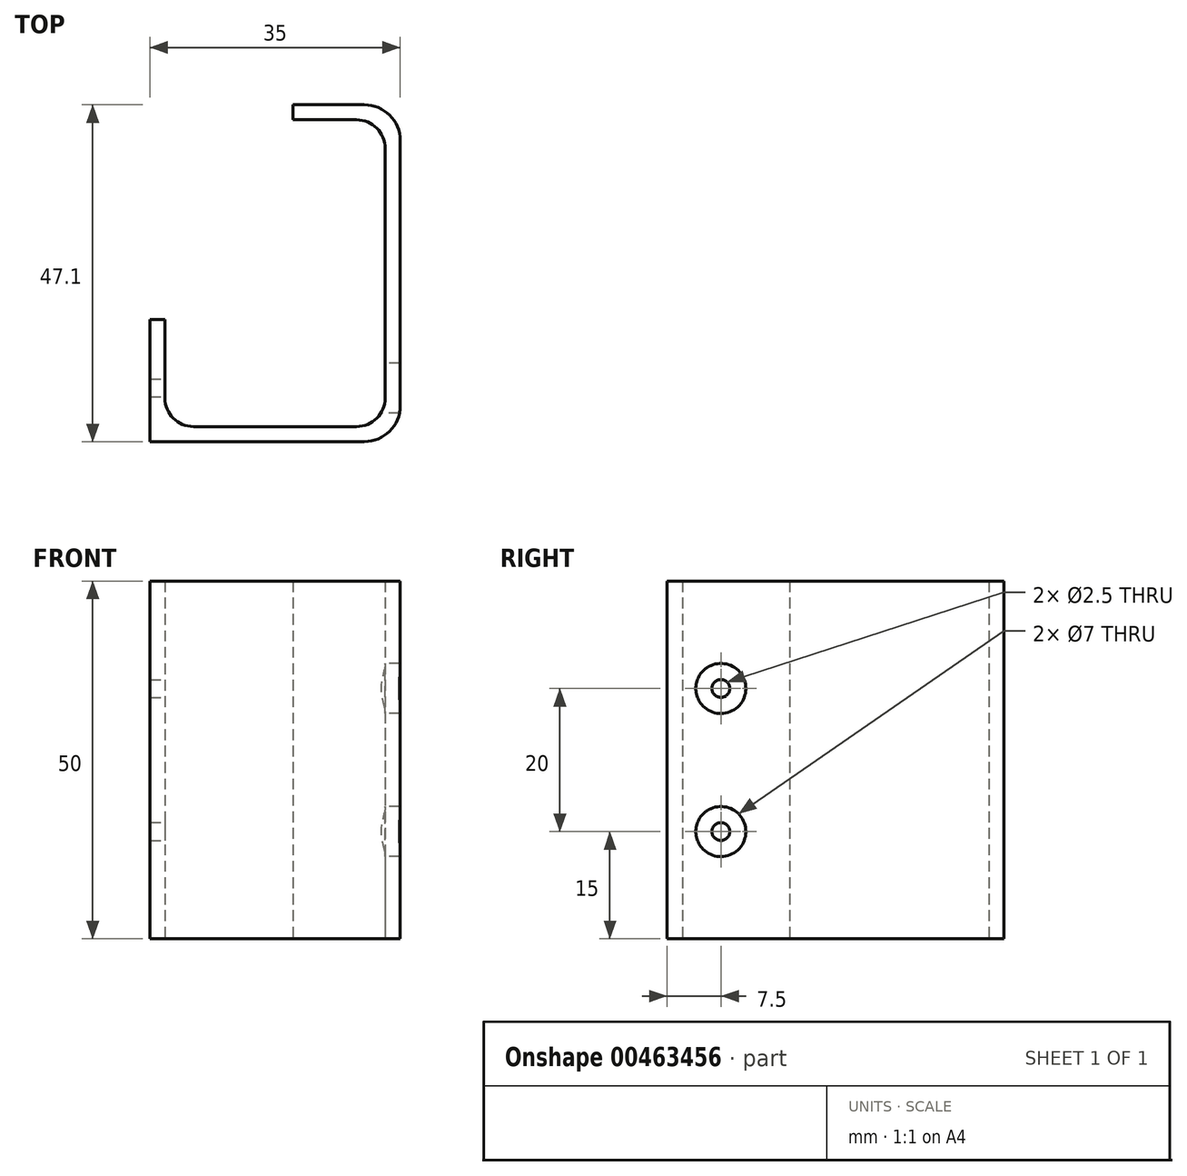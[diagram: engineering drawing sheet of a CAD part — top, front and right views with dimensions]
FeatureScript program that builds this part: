
annotation { "Feature Type Name" : "Feature", "Feature Type Description" : "" }
export const myFeature = defineFeature(function(context is Context, id is Id, definition is map)
    precondition{}
    {
        {
            var Q0;
            Q0=qCreatedBy(makeId("Top.planeOp"),FACE);
            var sketch = newSketch(context, id + "F0", { "sketchPlane" : qUnion([Q0])});
            skLineSegment(sketch, "E0", {"start": v(-4, 0) * mm, "end": v(-26.8, 0) * mm});
            skLineSegment(sketch, "E1", {"start": v(-30.8, 4) * mm, "end": v(-30.8, 45) * mm});
            skLineSegment(sketch, "E2", {"start": v(-30.8, 45) * mm, "end": v(-32.9, 45) * mm});
            skLineSegment(sketch, "E3", {"start": v(-32.9, 45) * mm, "end": v(-32.9, -2.1) * mm});
            skLineSegment(sketch, "E4", {"start": v(-32.9, -2.1) * mm, "end": v(2.1, -2.1) * mm});
            skLineSegment(sketch, "E5", {"start": v(2.1, -2.1) * mm, "end": v(2.1, 45) * mm});
            skPoint(sketch, "E6.end.orphan", {"position": v(14.76, 0) * mm});
            skLineSegment(sketch, "E7", {"start": v(2.1, 45) * mm, "end": v(-12.9, 45) * mm});
            skLineSegment(sketch, "E8", {"start": v(-12.9, 45) * mm, "end": v(-12.9, 42.9) * mm});
            skLineSegment(sketch, "E9", {"start": v(-12.9, 42.9) * mm, "end": v(-4, 42.9) * mm});
            skLineSegment(sketch, "E10", {"start": v(0, 38.9) * mm, "end": v(0, 4) * mm});
            skPoint(sketch, "E11.visualSharp", {"position": v(0, 42.9) * mm});
            skArc(sketch, "E11.filletArc", {"start": v(0, 38.9) * mm, "mid": v(-1.17, 41.73) * mm, "end": v(-4, 42.9) * mm});
            skPoint(sketch, "E12.visualSharp", {"position": v(-30.8, 0) * mm});
            skArc(sketch, "E12.filletArc", {"start": v(-30.8, 4) * mm, "mid": v(-29.63, 1.17) * mm, "end": v(-26.8, 0) * mm});
            skPoint(sketch, "E13.visualSharp", {"position": v(0, 0) * mm});
            skArc(sketch, "E13.filletArc", {"start": v(-4, 0) * mm, "mid": v(-1.17, 1.17) * mm, "end": v(0, 4) * mm});
            skLineSegment(sketch, "E14", {"start": v(-24.73, 0) * mm, "end": v(-24.73, 15) * mm, "construction": true});
            skLineSegment(sketch, "E15", {"start": v(-30.8, 15) * mm, "end": v(-32.9, 15) * mm});
            skSolve(sketch);
        }
        {
            var Q0;
            Q0=makeQuery(id+"F0.imprint","IMPRINT",FACE,{"disambiguationData":[TD([[makeQuery(id+"F0.imprint","IMPRINT",EDGE,{"derivedFrom":sQuery(id+"F0.wireOp",EDGE,"E0")}),1.0]])]});
            extrude(context, id + "F1", {"entities" : qUnion([Q0]), "depth" : 50 * mm});
        }
        {
            var Q0;
            Q0=qCreatedBy(makeId("Right.planeOp"),FACE);
            var sketch = newSketch(context, id + "F2", { "sketchPlane" : qUnion([Q0])});
            skLineSegment(sketch, "E16", {"start": v(0, 0) * mm, "end": v(5.4, 0) * mm, "construction": true});
            skLineSegment(sketch, "E17", {"start": v(5.4, 0) * mm, "end": v(5.4, 15) * mm, "construction": true});
            skLineSegment(sketch, "E18", {"start": v(5.4, 15) * mm, "end": v(5.4, 35) * mm, "construction": true});
            skLineSegment(sketch, "E19", {"start": v(5.4, 35) * mm, "end": v(5.4, 50) * mm, "construction": true});
            skCircle(sketch, "E20", {"center": v(5.4, 35) * mm, "radius": 1.25 * mm});
            skCircle(sketch, "E21", {"center": v(5.4, 15) * mm, "radius": 1.25 * mm});
            skCircle(sketch, "E22", {"center": v(5.4, 15) * mm, "radius": 3.5 * mm});
            skCircle(sketch, "E23", {"center": v(5.4, 35) * mm, "radius": 3.5 * mm});
            skSolve(sketch);
        }
        {
            var Q0;
            Q0=makeQuery(id+"F2.imprint","IMPRINT",FACE,{"disambiguationData":[TD([[makeQuery(id+"F2.imprint","IMPRINT",EDGE,{"derivedFrom":sQuery(id+"F2.wireOp",EDGE,"E20")}),1.0]])]});
            var Q1;
            Q1=makeQuery(id+"F2.imprint","IMPRINT",FACE,{"disambiguationData":[TD([[makeQuery(id+"F2.imprint","IMPRINT",EDGE,{"derivedFrom":sQuery(id+"F2.wireOp",EDGE,"E21")}),1.0]])]});
            extrude(context, id + "F3", {"entities" : qUnion([Q0, Q1]), "operationType" : NewBodyOperationType.REMOVE, "endBound" : BoundingType.THROUGH_ALL, "oppositeDirection" : true, "depth" : 25 * mm});
        }
        {
            var Q0;
            Q0=makeQuery(id+"F2.imprint","IMPRINT",FACE,{"disambiguationData":[TD([[makeQuery(id+"F2.imprint","IMPRINT",EDGE,{"derivedFrom":sQuery(id+"F2.wireOp",EDGE,"E20")}),-1.0]])]});
            var Q1;
            Q1=makeQuery(id+"F2.imprint","IMPRINT",FACE,{"disambiguationData":[TD([[makeQuery(id+"F2.imprint","IMPRINT",EDGE,{"derivedFrom":sQuery(id+"F2.wireOp",EDGE,"E21")}),-1.0]])]});
            var Q2;
            Q2=makeQuery(id+"F2.imprint","IMPRINT",FACE,{"disambiguationData":[TD([[makeQuery(id+"F2.imprint","IMPRINT",EDGE,{"derivedFrom":sQuery(id+"F2.wireOp",EDGE,"E21")}),1.0]])]});
            var Q3;
            Q3=makeQuery(id+"F2.imprint","IMPRINT",FACE,{"disambiguationData":[TD([[makeQuery(id+"F2.imprint","IMPRINT",EDGE,{"derivedFrom":sQuery(id+"F2.wireOp",EDGE,"E20")}),1.0]])]});
            extrude(context, id + "F4", {"entities" : qUnion([Q0, Q1, Q2, Q3]), "operationType" : NewBodyOperationType.REMOVE, "endBound" : BoundingType.UP_TO_NEXT, "depth" : 25 * mm, "hasSecondDirection" : true, "secondDirectionOppositeDirection" : true, "secondDirectionDepth" : 10 * mm});
        }
        {
            var Q0;
            Q0=makeQuery(id+"F1.opExtrude","SWEPT_EDGE",EDGE,{"disambiguationData":[OSD([sQuery(id+"F0.wireOp",EDGE,"E5"),sQuery(id+"F0.wireOp",EDGE,"E7")])]});
            var Q1;
            Q1=makeQuery(id+"F1.opExtrude","SWEPT_EDGE",EDGE,{"disambiguationData":[OSD([sQuery(id+"F0.wireOp",EDGE,"E4"),sQuery(id+"F0.wireOp",EDGE,"E5")])]});
            fillet(context, id + "F5", {"entities" : qUnion([Q0, Q1]), "radius" : 5 * mm, "tangentPropagation" : true, "allowEdgeOverflow" : false});
        }
    });
